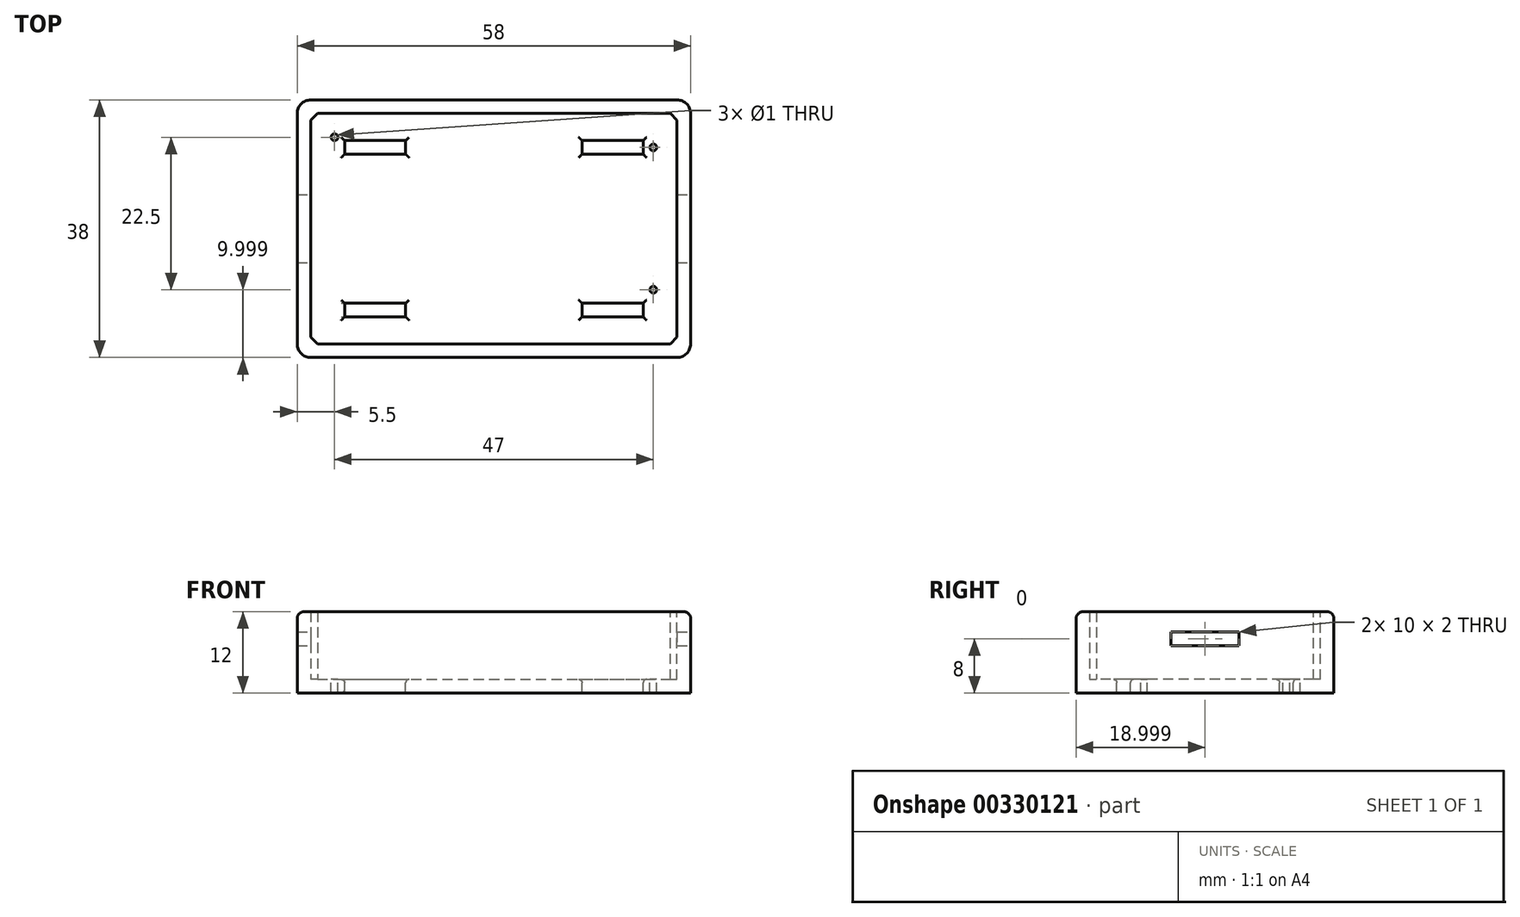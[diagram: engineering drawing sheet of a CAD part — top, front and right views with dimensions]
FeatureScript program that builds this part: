
annotation { "Feature Type Name" : "Feature", "Feature Type Description" : "" }
export const myFeature = defineFeature(function(context is Context, id is Id, definition is map)
    precondition{}
    {
        {
            var Q0;
            Q0=qCreatedBy(makeId("Top.planeOp"),FACE);
            var sketch = newSketch(context, id + "F0", { "sketchPlane" : qUnion([Q0])});
            skLineSegment(sketch, "E0.bottom", {"start": v(-47.3, 10.19) * mm, "end": v(10.7, 10.19) * mm});
            skLineSegment(sketch, "E0.top", {"start": v(-47.3, -27.81) * mm, "end": v(10.7, -27.81) * mm});
            skLineSegment(sketch, "E0.left", {"start": v(-47.3, 10.19) * mm, "end": v(-47.3, -27.81) * mm});
            skLineSegment(sketch, "E0.right", {"start": v(10.7, 10.19) * mm, "end": v(10.7, -27.81) * mm});
            skSolve(sketch);
        }
        {
            var Q0;
            Q0=qSketchRegion(id+"F0",true);
            extrude(context, id + "F1", {"entities" : qUnion([Q0]), "depth" : 2 * mm});
        }
        {
            var Q0;
            Q0=makeQuery(id+"F1.opExtrude","CAP_FACE",FACE,{"disambiguationData":[OSD([sQuery(id+"F0.wireOp",EDGE,"E0.bottom"),sQuery(id+"F0.wireOp",EDGE,"E0.top"),sQuery(id+"F0.wireOp",EDGE,"E0.left"),sQuery(id+"F0.wireOp",EDGE,"E0.right")])],"isStart":false});
            var sketch = newSketch(context, id + "F2", { "sketchPlane" : qUnion([Q0])});
            skLineSegment(sketch, "E1.bottom", {"start": v(-45.3, 8.19) * mm, "end": v(8.7, 8.19) * mm});
            skLineSegment(sketch, "E1.top", {"start": v(-45.3, -25.81) * mm, "end": v(8.7, -25.81) * mm});
            skLineSegment(sketch, "E1.left", {"start": v(-45.3, 8.19) * mm, "end": v(-45.3, -25.81) * mm});
            skLineSegment(sketch, "E1.right", {"start": v(8.7, 8.19) * mm, "end": v(8.7, -25.81) * mm});
            skSolve(sketch);
        }
        {
            var Q0;
            Q0=makeQuery(id+"F2.imprint","IMPRINT",FACE,{"disambiguationData":[TD([[makeQuery(id+"F2.imprint","IMPRINT",EDGE,{"derivedFrom":sQuery(id+"F2.wireOp",EDGE,"E1.bottom")}),1.0]])]});
            extrude(context, id + "F3", {"entities" : qUnion([Q0]), "operationType" : NewBodyOperationType.ADD, "depth" : 10 * mm});
        }
        {
            var Q0;
            Q0=qCreatedBy(makeId("Front.planeOp"),FACE);
            var sketch = newSketch(context, id + "F4", { "sketchPlane" : qUnion([Q0])});
            skLineSegment(sketch, "E2.bottom", {"start": v(-40.3, 6) * mm, "end": v(-31.3, 6) * mm});
            skLineSegment(sketch, "E2.top", {"start": v(-40.3, 4) * mm, "end": v(-31.3, 4) * mm});
            skLineSegment(sketch, "E2.left", {"start": v(-40.3, 6) * mm, "end": v(-40.3, 4) * mm});
            skLineSegment(sketch, "E2.right", {"start": v(-31.3, 6) * mm, "end": v(-31.3, 4) * mm});
            skLineSegment(sketch, "E3.bottom", {"start": v(-5.3, 6) * mm, "end": v(3.7, 6) * mm});
            skLineSegment(sketch, "E3.top", {"start": v(-5.3, 4) * mm, "end": v(3.7, 4) * mm});
            skLineSegment(sketch, "E3.left", {"start": v(-5.3, 6) * mm, "end": v(-5.3, 4) * mm});
            skLineSegment(sketch, "E3.right", {"start": v(3.7, 6) * mm, "end": v(3.7, 4) * mm});
            skSolve(sketch);
        }
        {
            var Q0;
            Q0=qCreatedBy(makeId("Top.planeOp"),FACE);
            var sketch = newSketch(context, id + "F5", { "sketchPlane" : qUnion([Q0])});
            skLineSegment(sketch, "E4.bottom", {"start": v(-40.3, -19.81) * mm, "end": v(-31.3, -19.81) * mm});
            skLineSegment(sketch, "E4.top", {"start": v(-40.3, -21.81) * mm, "end": v(-31.3, -21.81) * mm});
            skLineSegment(sketch, "E4.left", {"start": v(-40.3, -19.81) * mm, "end": v(-40.3, -21.81) * mm});
            skLineSegment(sketch, "E4.right", {"start": v(-31.3, -19.81) * mm, "end": v(-31.3, -21.81) * mm});
            skLineSegment(sketch, "E5.bottom", {"start": v(-40.3, 4.19) * mm, "end": v(-31.3, 4.19) * mm});
            skLineSegment(sketch, "E5.top", {"start": v(-40.3, 2.19) * mm, "end": v(-31.3, 2.19) * mm});
            skLineSegment(sketch, "E5.left", {"start": v(-40.3, 4.19) * mm, "end": v(-40.3, 2.19) * mm});
            skLineSegment(sketch, "E5.right", {"start": v(-31.3, 4.19) * mm, "end": v(-31.3, 2.19) * mm});
            skLineSegment(sketch, "E6.bottom", {"start": v(-5.3, 4.19) * mm, "end": v(3.7, 4.19) * mm});
            skLineSegment(sketch, "E6.top", {"start": v(-5.3, 2.19) * mm, "end": v(3.7, 2.19) * mm});
            skLineSegment(sketch, "E6.left", {"start": v(-5.3, 4.19) * mm, "end": v(-5.3, 2.19) * mm});
            skLineSegment(sketch, "E6.right", {"start": v(3.7, 4.19) * mm, "end": v(3.7, 2.19) * mm});
            skLineSegment(sketch, "E7.bottom", {"start": v(-5.3, -19.81) * mm, "end": v(3.7, -19.81) * mm});
            skLineSegment(sketch, "E7.top", {"start": v(-5.3, -21.81) * mm, "end": v(3.7, -21.81) * mm});
            skLineSegment(sketch, "E7.left", {"start": v(-5.3, -19.81) * mm, "end": v(-5.3, -21.81) * mm});
            skLineSegment(sketch, "E7.right", {"start": v(3.7, -19.81) * mm, "end": v(3.7, -21.81) * mm});
            skSolve(sketch);
        }
        {
            var Q0;
            Q0=qSketchRegion(id+"F5",true);
            extrude(context, id + "F6", {"entities" : qUnion([Q0]), "operationType" : NewBodyOperationType.REMOVE, "oppositeDirection" : true, "depth" : 25 * mm, "symmetric" : true});
        }
        {
            var Q0;
            {var subQ0=sQuery(id+"F0.wireOp",EDGE,"E0.left");var subQ1=sQuery(id+"F0.wireOp",EDGE,"E0.top");Q0=makeQuery(id+"F3.boolean.opBoolean","MERGE",EDGE,{"derivedFrom":[makeQuery(id+"F1.opExtrude","SWEPT_EDGE",EDGE,{"disambiguationData":[OSD([subQ1,subQ0])]}),makeQuery(id+"F3.opExtrude","SWEPT_EDGE",EDGE,{"disambiguationData":[OSD([subQ1,subQ0])]})]});}
            var Q1;
            {var subQ0=sQuery(id+"F0.wireOp",EDGE,"E0.right");var subQ1=sQuery(id+"F0.wireOp",EDGE,"E0.top");Q1=makeQuery(id+"F3.boolean.opBoolean","MERGE",EDGE,{"derivedFrom":[makeQuery(id+"F1.opExtrude","SWEPT_EDGE",EDGE,{"disambiguationData":[OSD([subQ1,subQ0])]}),makeQuery(id+"F3.opExtrude","SWEPT_EDGE",EDGE,{"disambiguationData":[OSD([subQ1,subQ0])]})]});}
            var Q2;
            {var subQ0=sQuery(id+"F0.wireOp",EDGE,"E0.right");var subQ1=sQuery(id+"F0.wireOp",EDGE,"E0.bottom");Q2=makeQuery(id+"F3.boolean.opBoolean","MERGE",EDGE,{"derivedFrom":[makeQuery(id+"F1.opExtrude","SWEPT_EDGE",EDGE,{"disambiguationData":[OSD([subQ1,subQ0])]}),makeQuery(id+"F3.opExtrude","SWEPT_EDGE",EDGE,{"disambiguationData":[OSD([subQ1,subQ0])]})]});}
            var Q3;
            {var subQ0=sQuery(id+"F0.wireOp",EDGE,"E0.left");var subQ1=sQuery(id+"F0.wireOp",EDGE,"E0.bottom");Q3=makeQuery(id+"F3.boolean.opBoolean","MERGE",EDGE,{"derivedFrom":[makeQuery(id+"F1.opExtrude","SWEPT_EDGE",EDGE,{"disambiguationData":[OSD([subQ1,subQ0])]}),makeQuery(id+"F3.opExtrude","SWEPT_EDGE",EDGE,{"disambiguationData":[OSD([subQ1,subQ0])]})]});}
            fillet(context, id + "F7", {"entities" : qUnion([Q0, Q1, Q2, Q3]), "radius" : 2 * mm, "tangentPropagation" : true, "allowEdgeOverflow" : false});
        }
        {
            var Q0;
            {var subQ0=sQuery(id+"F0.wireOp",EDGE,"E0.top");Q0=makeQuery(id+"FAcmGurFxiyDa2V_1.boolean.opBoolean","INTERSECT",EDGE,{"derivedFrom":[makeQuery(id+"F3.boolean.opBoolean","MERGE",FACE,{"derivedFrom":[makeQuery(id+"F1.opExtrude","SWEPT_FACE",FACE,{"disambiguationData":[OSD([subQ0])]}),makeQuery(id+"F3.opExtrude","SWEPT_FACE",FACE,{"disambiguationData":[OSD([subQ0])]})]}),makeQuery(id+"FAcmGurFxiyDa2V_1.opExtrude","SWEPT_FACE",FACE,{"disambiguationData":[OSD([sQuery(id+"F4.wireOp",EDGE,"E2.top")])]})]});}
            var Q1;
            {var subQ0=sQuery(id+"F0.wireOp",EDGE,"E0.top");Q1=makeQuery(id+"FAcmGurFxiyDa2V_1.boolean.opBoolean","INTERSECT",EDGE,{"derivedFrom":[makeQuery(id+"F3.boolean.opBoolean","MERGE",FACE,{"derivedFrom":[makeQuery(id+"F1.opExtrude","SWEPT_FACE",FACE,{"disambiguationData":[OSD([subQ0])]}),makeQuery(id+"F3.opExtrude","SWEPT_FACE",FACE,{"disambiguationData":[OSD([subQ0])]})]}),makeQuery(id+"FAcmGurFxiyDa2V_1.opExtrude","SWEPT_FACE",FACE,{"disambiguationData":[OSD([sQuery(id+"F4.wireOp",EDGE,"E2.left")])]})]});}
            var Q2;
            {var subQ0=sQuery(id+"F0.wireOp",EDGE,"E0.top");Q2=makeQuery(id+"FAcmGurFxiyDa2V_1.boolean.opBoolean","INTERSECT",EDGE,{"derivedFrom":[makeQuery(id+"F3.boolean.opBoolean","MERGE",FACE,{"derivedFrom":[makeQuery(id+"F1.opExtrude","SWEPT_FACE",FACE,{"disambiguationData":[OSD([subQ0])]}),makeQuery(id+"F3.opExtrude","SWEPT_FACE",FACE,{"disambiguationData":[OSD([subQ0])]})]}),makeQuery(id+"FAcmGurFxiyDa2V_1.opExtrude","SWEPT_FACE",FACE,{"disambiguationData":[OSD([sQuery(id+"F4.wireOp",EDGE,"E2.bottom")])]})]});}
            var Q3;
            {var subQ0=sQuery(id+"F0.wireOp",EDGE,"E0.top");Q3=makeQuery(id+"FAcmGurFxiyDa2V_1.boolean.opBoolean","INTERSECT",EDGE,{"derivedFrom":[makeQuery(id+"F3.boolean.opBoolean","MERGE",FACE,{"derivedFrom":[makeQuery(id+"F1.opExtrude","SWEPT_FACE",FACE,{"disambiguationData":[OSD([subQ0])]}),makeQuery(id+"F3.opExtrude","SWEPT_FACE",FACE,{"disambiguationData":[OSD([subQ0])]})]}),makeQuery(id+"FAcmGurFxiyDa2V_1.opExtrude","SWEPT_FACE",FACE,{"disambiguationData":[OSD([sQuery(id+"F4.wireOp",EDGE,"E2.right")])]})]});}
            var Q4;
            {var subQ0=sQuery(id+"F0.wireOp",EDGE,"E0.top");Q4=makeQuery(id+"FAcmGurFxiyDa2V_1.boolean.opBoolean","INTERSECT",EDGE,{"derivedFrom":[makeQuery(id+"F3.boolean.opBoolean","MERGE",FACE,{"derivedFrom":[makeQuery(id+"F1.opExtrude","SWEPT_FACE",FACE,{"disambiguationData":[OSD([subQ0])]}),makeQuery(id+"F3.opExtrude","SWEPT_FACE",FACE,{"disambiguationData":[OSD([subQ0])]})]}),makeQuery(id+"FAcmGurFxiyDa2V_1.opExtrude","SWEPT_FACE",FACE,{"disambiguationData":[OSD([sQuery(id+"F4.wireOp",EDGE,"E3.left")])]})]});}
            var Q5;
            {var subQ0=sQuery(id+"F0.wireOp",EDGE,"E0.top");Q5=makeQuery(id+"FAcmGurFxiyDa2V_1.boolean.opBoolean","INTERSECT",EDGE,{"derivedFrom":[makeQuery(id+"F3.boolean.opBoolean","MERGE",FACE,{"derivedFrom":[makeQuery(id+"F1.opExtrude","SWEPT_FACE",FACE,{"disambiguationData":[OSD([subQ0])]}),makeQuery(id+"F3.opExtrude","SWEPT_FACE",FACE,{"disambiguationData":[OSD([subQ0])]})]}),makeQuery(id+"FAcmGurFxiyDa2V_1.opExtrude","SWEPT_FACE",FACE,{"disambiguationData":[OSD([sQuery(id+"F4.wireOp",EDGE,"E3.top")])]})]});}
            var Q6;
            {var subQ0=sQuery(id+"F0.wireOp",EDGE,"E0.top");Q6=makeQuery(id+"FAcmGurFxiyDa2V_1.boolean.opBoolean","INTERSECT",EDGE,{"derivedFrom":[makeQuery(id+"F3.boolean.opBoolean","MERGE",FACE,{"derivedFrom":[makeQuery(id+"F1.opExtrude","SWEPT_FACE",FACE,{"disambiguationData":[OSD([subQ0])]}),makeQuery(id+"F3.opExtrude","SWEPT_FACE",FACE,{"disambiguationData":[OSD([subQ0])]})]}),makeQuery(id+"FAcmGurFxiyDa2V_1.opExtrude","SWEPT_FACE",FACE,{"disambiguationData":[OSD([sQuery(id+"F4.wireOp",EDGE,"E3.right")])]})]});}
            var Q7;
            {var subQ0=sQuery(id+"F0.wireOp",EDGE,"E0.top");Q7=makeQuery(id+"FAcmGurFxiyDa2V_1.boolean.opBoolean","INTERSECT",EDGE,{"derivedFrom":[makeQuery(id+"F3.boolean.opBoolean","MERGE",FACE,{"derivedFrom":[makeQuery(id+"F1.opExtrude","SWEPT_FACE",FACE,{"disambiguationData":[OSD([subQ0])]}),makeQuery(id+"F3.opExtrude","SWEPT_FACE",FACE,{"disambiguationData":[OSD([subQ0])]})]}),makeQuery(id+"FAcmGurFxiyDa2V_1.opExtrude","SWEPT_FACE",FACE,{"disambiguationData":[OSD([sQuery(id+"F4.wireOp",EDGE,"E3.bottom")])]})]});}
            var Q8;
            Q8=makeQuery(id+"F6.boolean.opBoolean","INTERSECT",EDGE,{"derivedFrom":[makeQuery(id+"F1.opExtrude","CAP_FACE",FACE,{"disambiguationData":[OSD([sQuery(id+"F0.wireOp",EDGE,"E0.bottom"),sQuery(id+"F0.wireOp",EDGE,"E0.top"),sQuery(id+"F0.wireOp",EDGE,"E0.left"),sQuery(id+"F0.wireOp",EDGE,"E0.right")])],"isStart":false}),makeQuery(id+"F6.opExtrude","SWEPT_FACE",FACE,{"disambiguationData":[OSD([sQuery(id+"F5.wireOp",EDGE,"E6.top")])]})]});
            var Q9;
            Q9=makeQuery(id+"F6.boolean.opBoolean","INTERSECT",EDGE,{"derivedFrom":[makeQuery(id+"F1.opExtrude","CAP_FACE",FACE,{"disambiguationData":[OSD([sQuery(id+"F0.wireOp",EDGE,"E0.bottom"),sQuery(id+"F0.wireOp",EDGE,"E0.top"),sQuery(id+"F0.wireOp",EDGE,"E0.left"),sQuery(id+"F0.wireOp",EDGE,"E0.right")])],"isStart":false}),makeQuery(id+"F6.opExtrude","SWEPT_FACE",FACE,{"disambiguationData":[OSD([sQuery(id+"F5.wireOp",EDGE,"E6.bottom")])]})]});
            var Q10;
            Q10=makeQuery(id+"F6.boolean.opBoolean","INTERSECT",EDGE,{"derivedFrom":[makeQuery(id+"F1.opExtrude","CAP_FACE",FACE,{"disambiguationData":[OSD([sQuery(id+"F0.wireOp",EDGE,"E0.bottom"),sQuery(id+"F0.wireOp",EDGE,"E0.top"),sQuery(id+"F0.wireOp",EDGE,"E0.left"),sQuery(id+"F0.wireOp",EDGE,"E0.right")])],"isStart":false}),makeQuery(id+"F6.opExtrude","SWEPT_FACE",FACE,{"disambiguationData":[OSD([sQuery(id+"F5.wireOp",EDGE,"E6.right")])]})]});
            var Q11;
            Q11=makeQuery(id+"F6.boolean.opBoolean","INTERSECT",EDGE,{"derivedFrom":[makeQuery(id+"F1.opExtrude","CAP_FACE",FACE,{"disambiguationData":[OSD([sQuery(id+"F0.wireOp",EDGE,"E0.bottom"),sQuery(id+"F0.wireOp",EDGE,"E0.top"),sQuery(id+"F0.wireOp",EDGE,"E0.left"),sQuery(id+"F0.wireOp",EDGE,"E0.right")])],"isStart":false}),makeQuery(id+"F6.opExtrude","SWEPT_FACE",FACE,{"disambiguationData":[OSD([sQuery(id+"F5.wireOp",EDGE,"E6.left")])]})]});
            var Q12;
            Q12=makeQuery(id+"FAcmGurFxiyDa2V_1.boolean.opBoolean","INTERSECT",EDGE,{"derivedFrom":[makeQuery(id+"F3.opExtrude","SWEPT_FACE",FACE,{"disambiguationData":[OSD([sQuery(id+"F2.wireOp",EDGE,"E1.bottom")])]}),makeQuery(id+"FAcmGurFxiyDa2V_1.opExtrude","SWEPT_FACE",FACE,{"disambiguationData":[OSD([sQuery(id+"F4.wireOp",EDGE,"E3.top")])]})]});
            var Q13;
            Q13=makeQuery(id+"FAcmGurFxiyDa2V_1.boolean.opBoolean","INTERSECT",EDGE,{"derivedFrom":[makeQuery(id+"F3.opExtrude","SWEPT_FACE",FACE,{"disambiguationData":[OSD([sQuery(id+"F2.wireOp",EDGE,"E1.bottom")])]}),makeQuery(id+"FAcmGurFxiyDa2V_1.opExtrude","SWEPT_FACE",FACE,{"disambiguationData":[OSD([sQuery(id+"F4.wireOp",EDGE,"E3.bottom")])]})]});
            var Q14;
            Q14=makeQuery(id+"FAcmGurFxiyDa2V_1.boolean.opBoolean","INTERSECT",EDGE,{"derivedFrom":[makeQuery(id+"F3.opExtrude","SWEPT_FACE",FACE,{"disambiguationData":[OSD([sQuery(id+"F2.wireOp",EDGE,"E1.bottom")])]}),makeQuery(id+"FAcmGurFxiyDa2V_1.opExtrude","SWEPT_FACE",FACE,{"disambiguationData":[OSD([sQuery(id+"F4.wireOp",EDGE,"E3.left")])]})]});
            var Q15;
            Q15=makeQuery(id+"FAcmGurFxiyDa2V_1.boolean.opBoolean","INTERSECT",EDGE,{"derivedFrom":[makeQuery(id+"F3.opExtrude","SWEPT_FACE",FACE,{"disambiguationData":[OSD([sQuery(id+"F2.wireOp",EDGE,"E1.bottom")])]}),makeQuery(id+"FAcmGurFxiyDa2V_1.opExtrude","SWEPT_FACE",FACE,{"disambiguationData":[OSD([sQuery(id+"F4.wireOp",EDGE,"E3.right")])]})]});
            var Q16;
            Q16=makeQuery(id+"FAcmGurFxiyDa2V_1.boolean.opBoolean","INTERSECT",EDGE,{"derivedFrom":[makeQuery(id+"F3.opExtrude","SWEPT_FACE",FACE,{"disambiguationData":[OSD([sQuery(id+"F2.wireOp",EDGE,"E1.bottom")])]}),makeQuery(id+"FAcmGurFxiyDa2V_1.opExtrude","SWEPT_FACE",FACE,{"disambiguationData":[OSD([sQuery(id+"F4.wireOp",EDGE,"E2.bottom")])]})]});
            var Q17;
            Q17=makeQuery(id+"FAcmGurFxiyDa2V_1.boolean.opBoolean","INTERSECT",EDGE,{"derivedFrom":[makeQuery(id+"F3.opExtrude","SWEPT_FACE",FACE,{"disambiguationData":[OSD([sQuery(id+"F2.wireOp",EDGE,"E1.bottom")])]}),makeQuery(id+"FAcmGurFxiyDa2V_1.opExtrude","SWEPT_FACE",FACE,{"disambiguationData":[OSD([sQuery(id+"F4.wireOp",EDGE,"E2.top")])]})]});
            var Q18;
            Q18=makeQuery(id+"FAcmGurFxiyDa2V_1.boolean.opBoolean","INTERSECT",EDGE,{"derivedFrom":[makeQuery(id+"F3.opExtrude","SWEPT_FACE",FACE,{"disambiguationData":[OSD([sQuery(id+"F2.wireOp",EDGE,"E1.bottom")])]}),makeQuery(id+"FAcmGurFxiyDa2V_1.opExtrude","SWEPT_FACE",FACE,{"disambiguationData":[OSD([sQuery(id+"F4.wireOp",EDGE,"E2.right")])]})]});
            var Q19;
            Q19=makeQuery(id+"FAcmGurFxiyDa2V_1.boolean.opBoolean","INTERSECT",EDGE,{"derivedFrom":[makeQuery(id+"F3.opExtrude","SWEPT_FACE",FACE,{"disambiguationData":[OSD([sQuery(id+"F2.wireOp",EDGE,"E1.bottom")])]}),makeQuery(id+"FAcmGurFxiyDa2V_1.opExtrude","SWEPT_FACE",FACE,{"disambiguationData":[OSD([sQuery(id+"F4.wireOp",EDGE,"E2.left")])]})]});
            var Q20;
            Q20=makeQuery(id+"F6.boolean.opBoolean","INTERSECT",EDGE,{"derivedFrom":[makeQuery(id+"F1.opExtrude","CAP_FACE",FACE,{"disambiguationData":[OSD([sQuery(id+"F0.wireOp",EDGE,"E0.bottom"),sQuery(id+"F0.wireOp",EDGE,"E0.top"),sQuery(id+"F0.wireOp",EDGE,"E0.left"),sQuery(id+"F0.wireOp",EDGE,"E0.right")])],"isStart":false}),makeQuery(id+"F6.opExtrude","SWEPT_FACE",FACE,{"disambiguationData":[OSD([sQuery(id+"F5.wireOp",EDGE,"E5.top")])]})]});
            var Q21;
            Q21=makeQuery(id+"F6.boolean.opBoolean","INTERSECT",EDGE,{"derivedFrom":[makeQuery(id+"F1.opExtrude","CAP_FACE",FACE,{"disambiguationData":[OSD([sQuery(id+"F0.wireOp",EDGE,"E0.bottom"),sQuery(id+"F0.wireOp",EDGE,"E0.top"),sQuery(id+"F0.wireOp",EDGE,"E0.left"),sQuery(id+"F0.wireOp",EDGE,"E0.right")])],"isStart":false}),makeQuery(id+"F6.opExtrude","SWEPT_FACE",FACE,{"disambiguationData":[OSD([sQuery(id+"F5.wireOp",EDGE,"E5.bottom")])]})]});
            var Q22;
            Q22=makeQuery(id+"F6.boolean.opBoolean","INTERSECT",EDGE,{"derivedFrom":[makeQuery(id+"F1.opExtrude","CAP_FACE",FACE,{"disambiguationData":[OSD([sQuery(id+"F0.wireOp",EDGE,"E0.bottom"),sQuery(id+"F0.wireOp",EDGE,"E0.top"),sQuery(id+"F0.wireOp",EDGE,"E0.left"),sQuery(id+"F0.wireOp",EDGE,"E0.right")])],"isStart":false}),makeQuery(id+"F6.opExtrude","SWEPT_FACE",FACE,{"disambiguationData":[OSD([sQuery(id+"F5.wireOp",EDGE,"E5.right")])]})]});
            var Q23;
            Q23=makeQuery(id+"F6.boolean.opBoolean","INTERSECT",EDGE,{"derivedFrom":[makeQuery(id+"F1.opExtrude","CAP_FACE",FACE,{"disambiguationData":[OSD([sQuery(id+"F0.wireOp",EDGE,"E0.bottom"),sQuery(id+"F0.wireOp",EDGE,"E0.top"),sQuery(id+"F0.wireOp",EDGE,"E0.left"),sQuery(id+"F0.wireOp",EDGE,"E0.right")])],"isStart":false}),makeQuery(id+"F6.opExtrude","SWEPT_FACE",FACE,{"disambiguationData":[OSD([sQuery(id+"F5.wireOp",EDGE,"E5.left")])]})]});
            var Q24;
            Q24=makeQuery(id+"F6.boolean.opBoolean","INTERSECT",EDGE,{"derivedFrom":[makeQuery(id+"F1.opExtrude","CAP_FACE",FACE,{"disambiguationData":[OSD([sQuery(id+"F0.wireOp",EDGE,"E0.bottom"),sQuery(id+"F0.wireOp",EDGE,"E0.top"),sQuery(id+"F0.wireOp",EDGE,"E0.left"),sQuery(id+"F0.wireOp",EDGE,"E0.right")])],"isStart":false}),makeQuery(id+"F6.opExtrude","SWEPT_FACE",FACE,{"disambiguationData":[OSD([sQuery(id+"F5.wireOp",EDGE,"E4.bottom")])]})]});
            var Q25;
            Q25=makeQuery(id+"F6.boolean.opBoolean","INTERSECT",EDGE,{"derivedFrom":[makeQuery(id+"F1.opExtrude","CAP_FACE",FACE,{"disambiguationData":[OSD([sQuery(id+"F0.wireOp",EDGE,"E0.bottom"),sQuery(id+"F0.wireOp",EDGE,"E0.top"),sQuery(id+"F0.wireOp",EDGE,"E0.left"),sQuery(id+"F0.wireOp",EDGE,"E0.right")])],"isStart":false}),makeQuery(id+"F6.opExtrude","SWEPT_FACE",FACE,{"disambiguationData":[OSD([sQuery(id+"F5.wireOp",EDGE,"E4.top")])]})]});
            var Q26;
            Q26=makeQuery(id+"F6.boolean.opBoolean","INTERSECT",EDGE,{"derivedFrom":[makeQuery(id+"F1.opExtrude","CAP_FACE",FACE,{"disambiguationData":[OSD([sQuery(id+"F0.wireOp",EDGE,"E0.bottom"),sQuery(id+"F0.wireOp",EDGE,"E0.top"),sQuery(id+"F0.wireOp",EDGE,"E0.left"),sQuery(id+"F0.wireOp",EDGE,"E0.right")])],"isStart":true}),makeQuery(id+"F6.opExtrude","SWEPT_FACE",FACE,{"disambiguationData":[OSD([sQuery(id+"F5.wireOp",EDGE,"E4.left")])]})]});
            var Q27;
            Q27=makeQuery(id+"F6.boolean.opBoolean","INTERSECT",EDGE,{"derivedFrom":[makeQuery(id+"F1.opExtrude","CAP_FACE",FACE,{"disambiguationData":[OSD([sQuery(id+"F0.wireOp",EDGE,"E0.bottom"),sQuery(id+"F0.wireOp",EDGE,"E0.top"),sQuery(id+"F0.wireOp",EDGE,"E0.left"),sQuery(id+"F0.wireOp",EDGE,"E0.right")])],"isStart":false}),makeQuery(id+"F6.opExtrude","SWEPT_FACE",FACE,{"disambiguationData":[OSD([sQuery(id+"F5.wireOp",EDGE,"E4.right")])]})]});
            var Q28;
            Q28=makeQuery(id+"F6.boolean.opBoolean","INTERSECT",EDGE,{"derivedFrom":[makeQuery(id+"F1.opExtrude","CAP_FACE",FACE,{"disambiguationData":[OSD([sQuery(id+"F0.wireOp",EDGE,"E0.bottom"),sQuery(id+"F0.wireOp",EDGE,"E0.top"),sQuery(id+"F0.wireOp",EDGE,"E0.left"),sQuery(id+"F0.wireOp",EDGE,"E0.right")])],"isStart":false}),makeQuery(id+"F6.opExtrude","SWEPT_FACE",FACE,{"disambiguationData":[OSD([sQuery(id+"F5.wireOp",EDGE,"E4.left")])]})]});
            var Q29;
            Q29=makeQuery(id+"F6.boolean.opBoolean","INTERSECT",EDGE,{"derivedFrom":[makeQuery(id+"F1.opExtrude","CAP_FACE",FACE,{"disambiguationData":[OSD([sQuery(id+"F0.wireOp",EDGE,"E0.bottom"),sQuery(id+"F0.wireOp",EDGE,"E0.top"),sQuery(id+"F0.wireOp",EDGE,"E0.left"),sQuery(id+"F0.wireOp",EDGE,"E0.right")])],"isStart":false}),makeQuery(id+"F6.opExtrude","SWEPT_FACE",FACE,{"disambiguationData":[OSD([sQuery(id+"F5.wireOp",EDGE,"E7.top")])]})]});
            var Q30;
            Q30=makeQuery(id+"F6.boolean.opBoolean","INTERSECT",EDGE,{"derivedFrom":[makeQuery(id+"F1.opExtrude","CAP_FACE",FACE,{"disambiguationData":[OSD([sQuery(id+"F0.wireOp",EDGE,"E0.bottom"),sQuery(id+"F0.wireOp",EDGE,"E0.top"),sQuery(id+"F0.wireOp",EDGE,"E0.left"),sQuery(id+"F0.wireOp",EDGE,"E0.right")])],"isStart":false}),makeQuery(id+"F6.opExtrude","SWEPT_FACE",FACE,{"disambiguationData":[OSD([sQuery(id+"F5.wireOp",EDGE,"E7.bottom")])]})]});
            var Q31;
            Q31=makeQuery(id+"F6.boolean.opBoolean","INTERSECT",EDGE,{"derivedFrom":[makeQuery(id+"F1.opExtrude","CAP_FACE",FACE,{"disambiguationData":[OSD([sQuery(id+"F0.wireOp",EDGE,"E0.bottom"),sQuery(id+"F0.wireOp",EDGE,"E0.top"),sQuery(id+"F0.wireOp",EDGE,"E0.left"),sQuery(id+"F0.wireOp",EDGE,"E0.right")])],"isStart":false}),makeQuery(id+"F6.opExtrude","SWEPT_FACE",FACE,{"disambiguationData":[OSD([sQuery(id+"F5.wireOp",EDGE,"E7.left")])]})]});
            var Q32;
            Q32=makeQuery(id+"F6.boolean.opBoolean","INTERSECT",EDGE,{"derivedFrom":[makeQuery(id+"F1.opExtrude","CAP_FACE",FACE,{"disambiguationData":[OSD([sQuery(id+"F0.wireOp",EDGE,"E0.bottom"),sQuery(id+"F0.wireOp",EDGE,"E0.top"),sQuery(id+"F0.wireOp",EDGE,"E0.left"),sQuery(id+"F0.wireOp",EDGE,"E0.right")])],"isStart":false}),makeQuery(id+"F6.opExtrude","SWEPT_FACE",FACE,{"disambiguationData":[OSD([sQuery(id+"F5.wireOp",EDGE,"E7.right")])]})]});
            var Q33;
            {var subQ0=sQuery(id+"F0.wireOp",EDGE,"E0.bottom");Q33=makeQuery(id+"FAcmGurFxiyDa2V_1.boolean.opBoolean","INTERSECT",EDGE,{"derivedFrom":[makeQuery(id+"F3.boolean.opBoolean","MERGE",FACE,{"derivedFrom":[makeQuery(id+"F1.opExtrude","SWEPT_FACE",FACE,{"disambiguationData":[OSD([subQ0])]}),makeQuery(id+"F3.opExtrude","SWEPT_FACE",FACE,{"disambiguationData":[OSD([subQ0])]})]}),makeQuery(id+"FAcmGurFxiyDa2V_1.opExtrude","SWEPT_FACE",FACE,{"disambiguationData":[OSD([sQuery(id+"F4.wireOp",EDGE,"E3.bottom")])]})]});}
            var Q34;
            {var subQ0=sQuery(id+"F0.wireOp",EDGE,"E0.bottom");Q34=makeQuery(id+"FAcmGurFxiyDa2V_1.boolean.opBoolean","INTERSECT",EDGE,{"derivedFrom":[makeQuery(id+"F3.boolean.opBoolean","MERGE",FACE,{"derivedFrom":[makeQuery(id+"F1.opExtrude","SWEPT_FACE",FACE,{"disambiguationData":[OSD([subQ0])]}),makeQuery(id+"F3.opExtrude","SWEPT_FACE",FACE,{"disambiguationData":[OSD([subQ0])]})]}),makeQuery(id+"FAcmGurFxiyDa2V_1.opExtrude","SWEPT_FACE",FACE,{"disambiguationData":[OSD([sQuery(id+"F4.wireOp",EDGE,"E3.left")])]})]});}
            var Q35;
            {var subQ0=sQuery(id+"F0.wireOp",EDGE,"E0.bottom");Q35=makeQuery(id+"FAcmGurFxiyDa2V_1.boolean.opBoolean","INTERSECT",EDGE,{"derivedFrom":[makeQuery(id+"F3.boolean.opBoolean","MERGE",FACE,{"derivedFrom":[makeQuery(id+"F1.opExtrude","SWEPT_FACE",FACE,{"disambiguationData":[OSD([subQ0])]}),makeQuery(id+"F3.opExtrude","SWEPT_FACE",FACE,{"disambiguationData":[OSD([subQ0])]})]}),makeQuery(id+"FAcmGurFxiyDa2V_1.opExtrude","SWEPT_FACE",FACE,{"disambiguationData":[OSD([sQuery(id+"F4.wireOp",EDGE,"E3.top")])]})]});}
            var Q36;
            {var subQ0=sQuery(id+"F0.wireOp",EDGE,"E0.bottom");Q36=makeQuery(id+"FAcmGurFxiyDa2V_1.boolean.opBoolean","INTERSECT",EDGE,{"derivedFrom":[makeQuery(id+"F3.boolean.opBoolean","MERGE",FACE,{"derivedFrom":[makeQuery(id+"F1.opExtrude","SWEPT_FACE",FACE,{"disambiguationData":[OSD([subQ0])]}),makeQuery(id+"F3.opExtrude","SWEPT_FACE",FACE,{"disambiguationData":[OSD([subQ0])]})]}),makeQuery(id+"FAcmGurFxiyDa2V_1.opExtrude","SWEPT_FACE",FACE,{"disambiguationData":[OSD([sQuery(id+"F4.wireOp",EDGE,"E3.right")])]})]});}
            var Q37;
            {var subQ0=sQuery(id+"F0.wireOp",EDGE,"E0.bottom");Q37=makeQuery(id+"FAcmGurFxiyDa2V_1.boolean.opBoolean","INTERSECT",EDGE,{"derivedFrom":[makeQuery(id+"F3.boolean.opBoolean","MERGE",FACE,{"derivedFrom":[makeQuery(id+"F1.opExtrude","SWEPT_FACE",FACE,{"disambiguationData":[OSD([subQ0])]}),makeQuery(id+"F3.opExtrude","SWEPT_FACE",FACE,{"disambiguationData":[OSD([subQ0])]})]}),makeQuery(id+"FAcmGurFxiyDa2V_1.opExtrude","SWEPT_FACE",FACE,{"disambiguationData":[OSD([sQuery(id+"F4.wireOp",EDGE,"E2.left")])]})]});}
            var Q38;
            {var subQ0=sQuery(id+"F0.wireOp",EDGE,"E0.bottom");Q38=makeQuery(id+"FAcmGurFxiyDa2V_1.boolean.opBoolean","INTERSECT",EDGE,{"derivedFrom":[makeQuery(id+"F3.boolean.opBoolean","MERGE",FACE,{"derivedFrom":[makeQuery(id+"F1.opExtrude","SWEPT_FACE",FACE,{"disambiguationData":[OSD([subQ0])]}),makeQuery(id+"F3.opExtrude","SWEPT_FACE",FACE,{"disambiguationData":[OSD([subQ0])]})]}),makeQuery(id+"FAcmGurFxiyDa2V_1.opExtrude","SWEPT_FACE",FACE,{"disambiguationData":[OSD([sQuery(id+"F4.wireOp",EDGE,"E2.bottom")])]})]});}
            var Q39;
            {var subQ0=sQuery(id+"F0.wireOp",EDGE,"E0.bottom");Q39=makeQuery(id+"FAcmGurFxiyDa2V_1.boolean.opBoolean","INTERSECT",EDGE,{"derivedFrom":[makeQuery(id+"F3.boolean.opBoolean","MERGE",FACE,{"derivedFrom":[makeQuery(id+"F1.opExtrude","SWEPT_FACE",FACE,{"disambiguationData":[OSD([subQ0])]}),makeQuery(id+"F3.opExtrude","SWEPT_FACE",FACE,{"disambiguationData":[OSD([subQ0])]})]}),makeQuery(id+"FAcmGurFxiyDa2V_1.opExtrude","SWEPT_FACE",FACE,{"disambiguationData":[OSD([sQuery(id+"F4.wireOp",EDGE,"E2.top")])]})]});}
            var Q40;
            {var subQ0=sQuery(id+"F0.wireOp",EDGE,"E0.bottom");Q40=makeQuery(id+"FAcmGurFxiyDa2V_1.boolean.opBoolean","INTERSECT",EDGE,{"derivedFrom":[makeQuery(id+"F3.boolean.opBoolean","MERGE",FACE,{"derivedFrom":[makeQuery(id+"F1.opExtrude","SWEPT_FACE",FACE,{"disambiguationData":[OSD([subQ0])]}),makeQuery(id+"F3.opExtrude","SWEPT_FACE",FACE,{"disambiguationData":[OSD([subQ0])]})]}),makeQuery(id+"FAcmGurFxiyDa2V_1.opExtrude","SWEPT_FACE",FACE,{"disambiguationData":[OSD([sQuery(id+"F4.wireOp",EDGE,"E2.right")])]})]});}
            var Q41;
            Q41=makeQuery(id+"FAcmGurFxiyDa2V_1.boolean.opBoolean","INTERSECT",EDGE,{"derivedFrom":[makeQuery(id+"F3.opExtrude","SWEPT_FACE",FACE,{"disambiguationData":[OSD([sQuery(id+"F2.wireOp",EDGE,"E1.top")])]}),makeQuery(id+"FAcmGurFxiyDa2V_1.opExtrude","SWEPT_FACE",FACE,{"disambiguationData":[OSD([sQuery(id+"F4.wireOp",EDGE,"E2.right")])]})]});
            var Q42;
            Q42=makeQuery(id+"FAcmGurFxiyDa2V_1.boolean.opBoolean","INTERSECT",EDGE,{"derivedFrom":[makeQuery(id+"F3.opExtrude","SWEPT_FACE",FACE,{"disambiguationData":[OSD([sQuery(id+"F2.wireOp",EDGE,"E1.top")])]}),makeQuery(id+"FAcmGurFxiyDa2V_1.opExtrude","SWEPT_FACE",FACE,{"disambiguationData":[OSD([sQuery(id+"F4.wireOp",EDGE,"E2.top")])]})]});
            var Q43;
            Q43=makeQuery(id+"FAcmGurFxiyDa2V_1.boolean.opBoolean","INTERSECT",EDGE,{"derivedFrom":[makeQuery(id+"F3.opExtrude","SWEPT_FACE",FACE,{"disambiguationData":[OSD([sQuery(id+"F2.wireOp",EDGE,"E1.top")])]}),makeQuery(id+"FAcmGurFxiyDa2V_1.opExtrude","SWEPT_FACE",FACE,{"disambiguationData":[OSD([sQuery(id+"F4.wireOp",EDGE,"E2.left")])]})]});
            var Q44;
            Q44=makeQuery(id+"FAcmGurFxiyDa2V_1.boolean.opBoolean","INTERSECT",EDGE,{"derivedFrom":[makeQuery(id+"F3.opExtrude","SWEPT_FACE",FACE,{"disambiguationData":[OSD([sQuery(id+"F2.wireOp",EDGE,"E1.top")])]}),makeQuery(id+"FAcmGurFxiyDa2V_1.opExtrude","SWEPT_FACE",FACE,{"disambiguationData":[OSD([sQuery(id+"F4.wireOp",EDGE,"E2.bottom")])]})]});
            var Q45;
            Q45=makeQuery(id+"FAcmGurFxiyDa2V_1.boolean.opBoolean","INTERSECT",EDGE,{"derivedFrom":[makeQuery(id+"F3.opExtrude","SWEPT_FACE",FACE,{"disambiguationData":[OSD([sQuery(id+"F2.wireOp",EDGE,"E1.top")])]}),makeQuery(id+"FAcmGurFxiyDa2V_1.opExtrude","SWEPT_FACE",FACE,{"disambiguationData":[OSD([sQuery(id+"F4.wireOp",EDGE,"E3.top")])]})]});
            var Q46;
            Q46=makeQuery(id+"FAcmGurFxiyDa2V_1.boolean.opBoolean","INTERSECT",EDGE,{"derivedFrom":[makeQuery(id+"F3.opExtrude","SWEPT_FACE",FACE,{"disambiguationData":[OSD([sQuery(id+"F2.wireOp",EDGE,"E1.top")])]}),makeQuery(id+"FAcmGurFxiyDa2V_1.opExtrude","SWEPT_FACE",FACE,{"disambiguationData":[OSD([sQuery(id+"F4.wireOp",EDGE,"E3.right")])]})]});
            var Q47;
            Q47=makeQuery(id+"FAcmGurFxiyDa2V_1.boolean.opBoolean","INTERSECT",EDGE,{"derivedFrom":[makeQuery(id+"F3.opExtrude","SWEPT_FACE",FACE,{"disambiguationData":[OSD([sQuery(id+"F2.wireOp",EDGE,"E1.top")])]}),makeQuery(id+"FAcmGurFxiyDa2V_1.opExtrude","SWEPT_FACE",FACE,{"disambiguationData":[OSD([sQuery(id+"F4.wireOp",EDGE,"E3.bottom")])]})]});
            var Q48;
            Q48=makeQuery(id+"FAcmGurFxiyDa2V_1.boolean.opBoolean","INTERSECT",EDGE,{"derivedFrom":[makeQuery(id+"F3.opExtrude","SWEPT_FACE",FACE,{"disambiguationData":[OSD([sQuery(id+"F2.wireOp",EDGE,"E1.top")])]}),makeQuery(id+"FAcmGurFxiyDa2V_1.opExtrude","SWEPT_FACE",FACE,{"disambiguationData":[OSD([sQuery(id+"F4.wireOp",EDGE,"E3.left")])]})]});
            fillet(context, id + "F8", {"entities" : qUnion([Q0, Q1, Q2, Q3, Q4, Q5, Q6, Q7, Q8, Q9, Q10, Q11, Q12, Q13, Q14, Q15, Q16, Q17, Q18, Q19, Q20, Q21, Q22, Q23, Q24, Q25, Q26, Q27, Q28, Q29, Q30, Q31, Q32, Q33, Q34, Q35, Q36, Q37, Q38, Q39, Q40, Q41, Q42, Q43, Q44, Q45, Q46, Q47, Q48]), "radius" : 0.5 * mm, "tangentPropagation" : true, "allowEdgeOverflow" : false});
        }
        {
            var Q0;
            Q0=makeQuery(id+"F3.opExtrude","CAP_EDGE",EDGE,{"disambiguationData":[OSD([sQuery(id+"F0.wireOp",EDGE,"E0.left")])],"isStart":false});
            var Q1;
            Q1=makeQuery(id+"F3.opExtrude","CAP_EDGE",EDGE,{"disambiguationData":[OSD([sQuery(id+"F0.wireOp",EDGE,"E0.top")])],"isStart":false});
            var Q2;
            Q2=makeQuery(id+"F3.opExtrude","CAP_EDGE",EDGE,{"disambiguationData":[OSD([sQuery(id+"F0.wireOp",EDGE,"E0.right")])],"isStart":false});
            var Q3;
            Q3=makeQuery(id+"F3.opExtrude","CAP_EDGE",EDGE,{"disambiguationData":[OSD([sQuery(id+"F0.wireOp",EDGE,"E0.bottom")])],"isStart":false});
            fillet(context, id + "F9", {"entities" : qUnion([Q0, Q1, Q2, Q3]), "radius" : 1 * mm, "tangentPropagation" : true, "allowEdgeOverflow" : false});
        }
        {
            var Q0;
            {var subQ0=sQuery(id+"F0.wireOp",EDGE,"E0.right");Q0=makeQuery(id+"F3.boolean.opBoolean","MERGE",FACE,{"derivedFrom":[makeQuery(id+"F1.opExtrude","SWEPT_FACE",FACE,{"disambiguationData":[OSD([subQ0])]}),makeQuery(id+"F3.opExtrude","SWEPT_FACE",FACE,{"disambiguationData":[OSD([subQ0])]})]});}
            var sketch = newSketch(context, id + "F10", { "sketchPlane" : qUnion([Q0])});
            skLineSegment(sketch, "E8.bottom", {"start": v(-13.81, 9) * mm, "end": v(-3.81, 9) * mm});
            skLineSegment(sketch, "E8.top", {"start": v(-13.81, 7) * mm, "end": v(-3.81, 7) * mm});
            skLineSegment(sketch, "E8.left", {"start": v(-13.81, 9) * mm, "end": v(-13.81, 7) * mm});
            skLineSegment(sketch, "E8.right", {"start": v(-3.81, 9) * mm, "end": v(-3.81, 7) * mm});
            skSolve(sketch);
        }
        {
            var Q0;
            Q0 = qSketchRegion(id + "F10", true);
            extrude(context, id + "F11", {"entities" : qUnion([Q0]), "operationType" : NewBodyOperationType.REMOVE, "endBound" : BoundingType.THROUGH_ALL, "oppositeDirection" : true, "depth" : 25 * mm});
        }
        {
            var Q0;
            Q0=makeQuery(id+"F3.opExtrude","SWEPT_EDGE",EDGE,{"disambiguationData":[OSD([sQuery(id+"F2.wireOp",EDGE,"E1.bottom"),sQuery(id+"F2.wireOp",EDGE,"E1.left")])]});
            var Q1;
            Q1=makeQuery(id+"F3.opExtrude","SWEPT_EDGE",EDGE,{"disambiguationData":[OSD([sQuery(id+"F2.wireOp",EDGE,"E1.bottom"),sQuery(id+"F2.wireOp",EDGE,"E1.right")])]});
            var Q2;
            Q2=makeQuery(id+"F3.opExtrude","SWEPT_EDGE",EDGE,{"disambiguationData":[OSD([sQuery(id+"F2.wireOp",EDGE,"E1.top"),sQuery(id+"F2.wireOp",EDGE,"E1.left")])]});
            var Q3;
            Q3=makeQuery(id+"F3.opExtrude","SWEPT_EDGE",EDGE,{"disambiguationData":[OSD([sQuery(id+"F2.wireOp",EDGE,"E1.top"),sQuery(id+"F2.wireOp",EDGE,"E1.right")])]});
            chamfer(context, id + "F12", {"entities" : qUnion([Q0, Q1, Q2, Q3]), "width" : 1 * mm, "tangentPropagation" : true});
        }
        {
            var Q0;
            Q0=makeQuery(id+"F1.opExtrude","CAP_FACE",FACE,{"disambiguationData":[OSD([sQuery(id+"F0.wireOp",EDGE,"E0.bottom"),sQuery(id+"F0.wireOp",EDGE,"E0.top"),sQuery(id+"F0.wireOp",EDGE,"E0.left"),sQuery(id+"F0.wireOp",EDGE,"E0.right")])],"isStart":false});
            var sketch = newSketch(context, id + "F13", { "sketchPlane" : qUnion([Q0])});
            skLineSegment(sketch, "E9.bottom", {"start": v(-43.3, 6.19) * mm, "end": v(6.7, 6.19) * mm});
            skLineSegment(sketch, "E9.top", {"start": v(-43.3, -23.81) * mm, "end": v(6.7, -23.81) * mm});
            skLineSegment(sketch, "E9.left", {"start": v(-43.3, 6.19) * mm, "end": v(-43.3, -23.81) * mm});
            skLineSegment(sketch, "E9.right", {"start": v(6.7, 6.19) * mm, "end": v(6.7, -23.81) * mm});
            skSolve(sketch);
        }
        {
            var Q0;
            Q0=makeQuery(id+"F13.imprint","IMPRINT",FACE,{"disambiguationData":[TD([[makeQuery(id+"F13.imprint","IMPRINT",EDGE,{"derivedFrom":sQuery(id+"F13.wireOp",EDGE,"E9.bottom")}),1.0]])]});
            var sketch = newSketch(context, id + "F14", { "sketchPlane" : qUnion([Q0])});
            skCircle(sketch, "E10", {"center": v(-41.8, 4.69) * mm, "radius": 0.5 * mm});
            skCircle(sketch, "E11", {"center": v(5.2, 3.19) * mm, "radius": 0.5 * mm});
            skCircle(sketch, "E12", {"center": v(5.2, -17.81) * mm, "radius": 0.5 * mm});
            skSolve(sketch);
        }
        {
            var Q0;
            Q0 = qSketchRegion(id + "F14", true);
            extrude(context, id + "F15", {"entities" : qUnion([Q0]), "operationType" : NewBodyOperationType.REMOVE, "oppositeDirection" : true, "depth" : 25 * mm});
        }
    });
